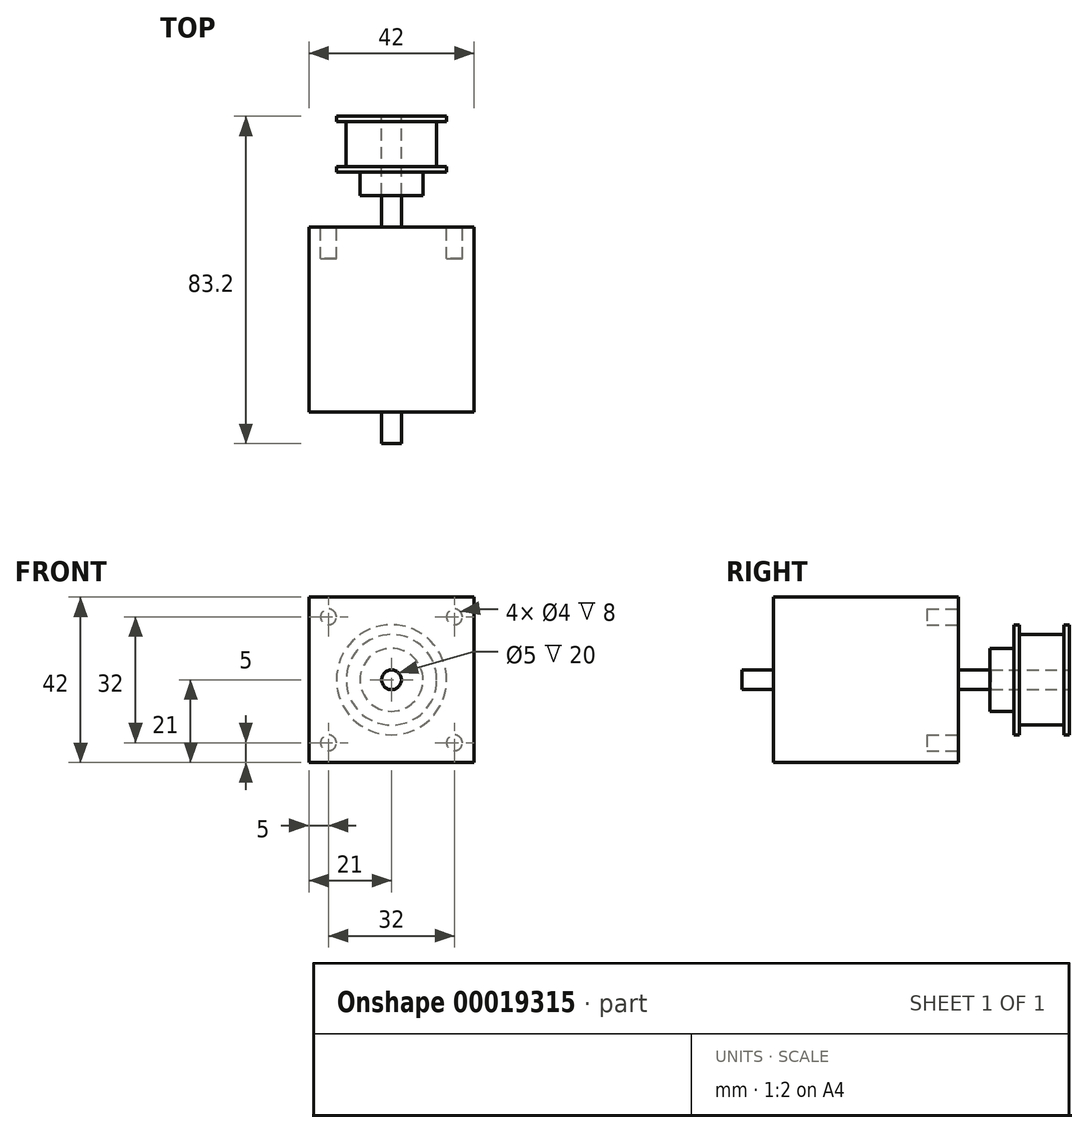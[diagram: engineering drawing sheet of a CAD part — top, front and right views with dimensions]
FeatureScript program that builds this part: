
annotation { "Feature Type Name" : "Feature", "Feature Type Description" : "" }
export const myFeature = defineFeature(function(context is Context, id is Id, definition is map)
    precondition{}
    {
        {
            var Q0;
            Q0=qCreatedBy(makeId("Front.planeOp"),FACE);
            var sketch = newSketch(context, id + "F0", { "sketchPlane" : qUnion([Q0])});
            skLineSegment(sketch, "E0.rect.bottom", {"start": v(21, -21) * mm, "end": v(-21, -21) * mm});
            skLineSegment(sketch, "E0.rect.top", {"start": v(21, 21) * mm, "end": v(-21, 21) * mm});
            skLineSegment(sketch, "E0.rect.left", {"start": v(21, -21) * mm, "end": v(21, 21) * mm});
            skLineSegment(sketch, "E0.rect.right", {"start": v(-21, -21) * mm, "end": v(-21, 21) * mm});
            skPoint(sketch, "E0.rect.middle", {"position": v(0, 0) * mm});
            skSolve(sketch);
        }
        {
            var Q0;
            Q0=qSketchRegion(id+"F0",true);
            extrude(context, id + "F1", {"entities" : qUnion([Q0]), "depth" : 47 * mm});
        }
        {
            var Q0;
            Q0=makeQuery(id+"F1.opExtrude","CAP_FACE",FACE,{"disambiguationData":[OSD([sQuery(id+"F0.wireOp",EDGE,"E0.rect.bottom"),sQuery(id+"F0.wireOp",EDGE,"E0.rect.top"),sQuery(id+"F0.wireOp",EDGE,"E0.rect.left"),sQuery(id+"F0.wireOp",EDGE,"E0.rect.right")])],"isStart":false});
            var sketch = newSketch(context, id + "F2", { "sketchPlane" : qUnion([Q0])});
            skCircle(sketch, "E1", {"center": v(0, 0) * mm, "radius": 2.5 * mm});
            skSolve(sketch);
        }
        {
            var Q0;
            Q0=qSketchRegion(id+"F2",true);
            extrude(context, id + "F3", {"entities" : qUnion([Q0]), "operationType" : NewBodyOperationType.ADD, "depth" : 8 * mm});
        }
        {
            var Q0;
            Q0=makeQuery(id+"F1.opExtrude","CAP_FACE",FACE,{"disambiguationData":[OSD([sQuery(id+"F0.wireOp",EDGE,"E0.rect.bottom"),sQuery(id+"F0.wireOp",EDGE,"E0.rect.top"),sQuery(id+"F0.wireOp",EDGE,"E0.rect.left"),sQuery(id+"F0.wireOp",EDGE,"E0.rect.right")])],"isStart":true});
            var sketch = newSketch(context, id + "F4", { "sketchPlane" : qUnion([Q0])});
            skCircle(sketch, "E2", {"center": v(0, 0) * mm, "radius": 2.5 * mm});
            skSolve(sketch);
        }
        {
            var Q0;
            Q0=qSketchRegion(id+"F4",true);
            extrude(context, id + "F5", {"entities" : qUnion([Q0]), "operationType" : NewBodyOperationType.ADD, "depth" : 24 * mm});
        }
        {
            var Q0;
            Q0=qCreatedBy(makeId("Front.planeOp"),FACE);
            cPlane(context, id + "F6", {"entities" : qUnion([Q0]), "cplaneType" : CPlaneType.OFFSET, "offset" : 8 * mm, "oppositeDirection" : true, "width" : 150 * mm, "height" : 150 * mm});
        }
        {
            var Q0;
            Q0=qCreatedBy(id+"F6.planeOp",FACE);
            var sketch = newSketch(context, id + "F7", { "sketchPlane" : qUnion([Q0])});
            skCircle(sketch, "E3", {"center": v(0, 0) * mm, "radius": 8 * mm});
            skSolve(sketch);
        }
        {
            var Q0;
            Q0=qSketchRegion(id+"F7",true);
            extrude(context, id + "F8", {"entities" : qUnion([Q0]), "oppositeDirection" : true, "depth" : 6 * mm});
        }
        {
            var Q0;
            Q0=makeQuery(id+"F8.opExtrude","CAP_FACE",FACE,{"disambiguationData":[OSD([sQuery(id+"F7.wireOp",EDGE,"E3")])],"isStart":false});
            var sketch = newSketch(context, id + "F9", { "sketchPlane" : qUnion([Q0])});
            skCircle(sketch, "E4", {"center": v(0, 0) * mm, "radius": 14 * mm});
            skSolve(sketch);
        }
        {
            var Q0;
            Q0=qSketchRegion(id+"F9",true);
            extrude(context, id + "F10", {"entities" : qUnion([Q0]), "operationType" : NewBodyOperationType.ADD, "depth" : 1.4 * mm});
        }
        {
            var Q0;
            Q0=makeQuery(id+"F10.opExtrude","CAP_FACE",FACE,{"disambiguationData":[OSD([sQuery(id+"F9.wireOp",EDGE,"E4")])],"isStart":false});
            var sketch = newSketch(context, id + "F11", { "sketchPlane" : qUnion([Q0])});
            skCircle(sketch, "E5", {"center": v(0, 0) * mm, "radius": 11.5 * mm});
            skSolve(sketch);
        }
        {
            var Q0;
            Q0=qSketchRegion(id+"F11",true);
            extrude(context, id + "F12", {"entities" : qUnion([Q0]), "operationType" : NewBodyOperationType.ADD, "depth" : 11.4 * mm});
        }
        {
            var Q0;
            Q0=makeQuery(id+"F12.opExtrude","CAP_FACE",FACE,{"disambiguationData":[OSD([sQuery(id+"F11.wireOp",EDGE,"E5")])],"isStart":false});
            var sketch = newSketch(context, id + "F13", { "sketchPlane" : qUnion([Q0])});
            skCircle(sketch, "E6", {"center": v(0, 0) * mm, "radius": 14 * mm});
            skSolve(sketch);
        }
        {
            var Q0;
            Q0=qSketchRegion(id+"F13",true);
            extrude(context, id + "F14", {"entities" : qUnion([Q0]), "operationType" : NewBodyOperationType.ADD, "depth" : 1.4 * mm});
        }
        {
            var Q0;
            Q0=makeQuery(id+"F14.opExtrude","CAP_FACE",FACE,{"disambiguationData":[OSD([sQuery(id+"F13.wireOp",EDGE,"E6")])],"isStart":false});
            var sketch = newSketch(context, id + "F15", { "sketchPlane" : qUnion([Q0])});
            skCircle(sketch, "E7", {"center": v(0, 0) * mm, "radius": 2.5 * mm});
            skSolve(sketch);
        }
        {
            var Q0;
            Q0=qSketchRegion(id+"F15",true);
            var Q1;
            Q1=makeQuery(id+"F1.opExtrude","CAP_FACE",FACE,{"disambiguationData":[OSD([sQuery(id+"F0.wireOp",EDGE,"E0.rect.bottom"),sQuery(id+"F0.wireOp",EDGE,"E0.rect.top"),sQuery(id+"F0.wireOp",EDGE,"E0.rect.left"),sQuery(id+"F0.wireOp",EDGE,"E0.rect.right")])],"isStart":true});
            extrude(context, id + "F16", {"entities" : qUnion([Q0]), "operationType" : NewBodyOperationType.REMOVE, "oppositeDirection" : true, "endBoundEntity" : qUnion([Q1]), "depth" : 20 * mm});
        }
        {
            var Q0;
            Q0=makeQuery(id+"F1.opExtrude","CAP_FACE",FACE,{"disambiguationData":[OSD([sQuery(id+"F0.wireOp",EDGE,"E0.rect.bottom"),sQuery(id+"F0.wireOp",EDGE,"E0.rect.top"),sQuery(id+"F0.wireOp",EDGE,"E0.rect.left"),sQuery(id+"F0.wireOp",EDGE,"E0.rect.right")])],"isStart":true});
            var sketch = newSketch(context, id + "F17", { "sketchPlane" : qUnion([Q0])});
            skLineSegment(sketch, "E8", {"start": v(-21, 21) * mm, "end": v(21, -21) * mm, "construction": true});
            skLineSegment(sketch, "E9", {"start": v(21, 21) * mm, "end": v(-21, -21) * mm, "construction": true});
            skCircle(sketch, "E10", {"center": v(-16, 16) * mm, "radius": 2 * mm});
            skLineSegment(sketch, "E11", {"start": v(-21, 0) * mm, "end": v(21, 0) * mm, "construction": true});
            skLineSegment(sketch, "E12", {"start": v(0, 21) * mm, "end": v(0, -21) * mm, "construction": true});
            skCircle(sketch, "E13.0.MirrorC", {"center": v(16, 16) * mm, "radius": 2 * mm});
            skCircle(sketch, "E14.0.MirrorC", {"center": v(-16, -16) * mm, "radius": 2 * mm});
            skCircle(sketch, "E15.0.MirrorC", {"center": v(16, -16) * mm, "radius": 2 * mm});
            skSolve(sketch);
        }
        {
            var Q0;
            Q0=qSketchRegion(id+"F17",true);
            extrude(context, id + "F18", {"entities" : qUnion([Q0]), "operationType" : NewBodyOperationType.REMOVE, "oppositeDirection" : true, "depth" : 8 * mm});
        }
    });
